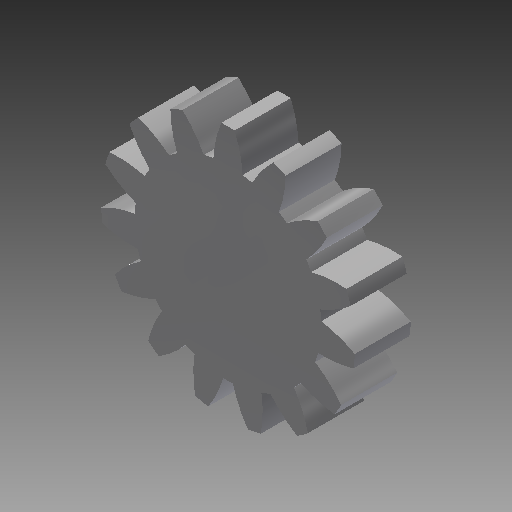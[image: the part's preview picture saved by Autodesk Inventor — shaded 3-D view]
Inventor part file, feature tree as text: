
AUTODESK INVENTOR PART (.ipt)
format: ipt  version: 2017 (Build 210142000, 142)  size: 197,120 bytes
history: native  units: mm (DEFAULTED — no unit token found)
features: plane x3, other x3, sketch x2, extrude x1
ambient origin geometry x8: Origin, YZ Plane, XZ Plane, XY Plane, X Axis, Y Axis, Z Axis, Center Point
bodies: Solid1 (feature_tree)
feature tree (9):
  extrude  "Extrusion1"  Depth=6.35mm TaperAngle=0.0deg
  plane  "Work Plane1"
  plane  "Work Plane2"
  plane  "Work Plane3"
  other  "Spur Gear"
  sketch  "Sketch1"  dims[d0=28.786667mm d1=6.35mm d2=0.0mm]
  sketch  "Sketch2"  dims[d3=25.4mm d4=76.2mm d5=0.0mm d6=0.0mm d7=2.094395mm d9=0.0mm d14=0.0mm d15=161.713333mm d16=0.0mm d17=0.0mm d18=0.0mm d19=161.713333mm]
  other  "Srf1"
  other  "Pitch Diameter"
